# Revit family: RP_Bidet_BW563Y_TEU
name_source: partatom
category: 衛生器具
units: mm (PartAtom-declared; Revit-internal decimal feet)

## family parameters
OmniClass タイトル = Sanitary, Laundry, and Cleaning Equipment
OmniClass 番号 = 23.45.00.00
パーツ タイプ = 標準
ロード時にボイドで切り取り = いいえ
丸型コネクタ寸法 = 直径を使用
作業面ベース = いいえ
共有 = いいえ
常に垂直 = はい
部屋計算ポイント = いいえ

## types (2) — shared parameters
Finish = White
Height = 410  [stored 1.34514 ft]
Length = 640  [stored 2.09974 ft]
Material = Ceramic
Seat Included = いいえ
URL = https://www.toto.com
Width = 380
モデル = BW563Y#XW
排気配管 = いいえ
排水配管 = はい
水配管 = はい
温水配管 = いいえ
製造元 = TOTO LTD.
説明 = Back-to-wall Bidet

## per-type parameters (varying)
| type | Rough-in |
| Rough-in_Vertical | 200  [stored 0.656168 ft] |
| Rough-in_Horizontal | 180  [stored 0.590551 ft] |

note: [stored X ft] marks values corroborated as IEEE doubles in the binary element streams (Revit-internal decimal feet)

## geometry (parser evidence)
native form markers: Sweep x3
no freeform markers — native parametric forms only
